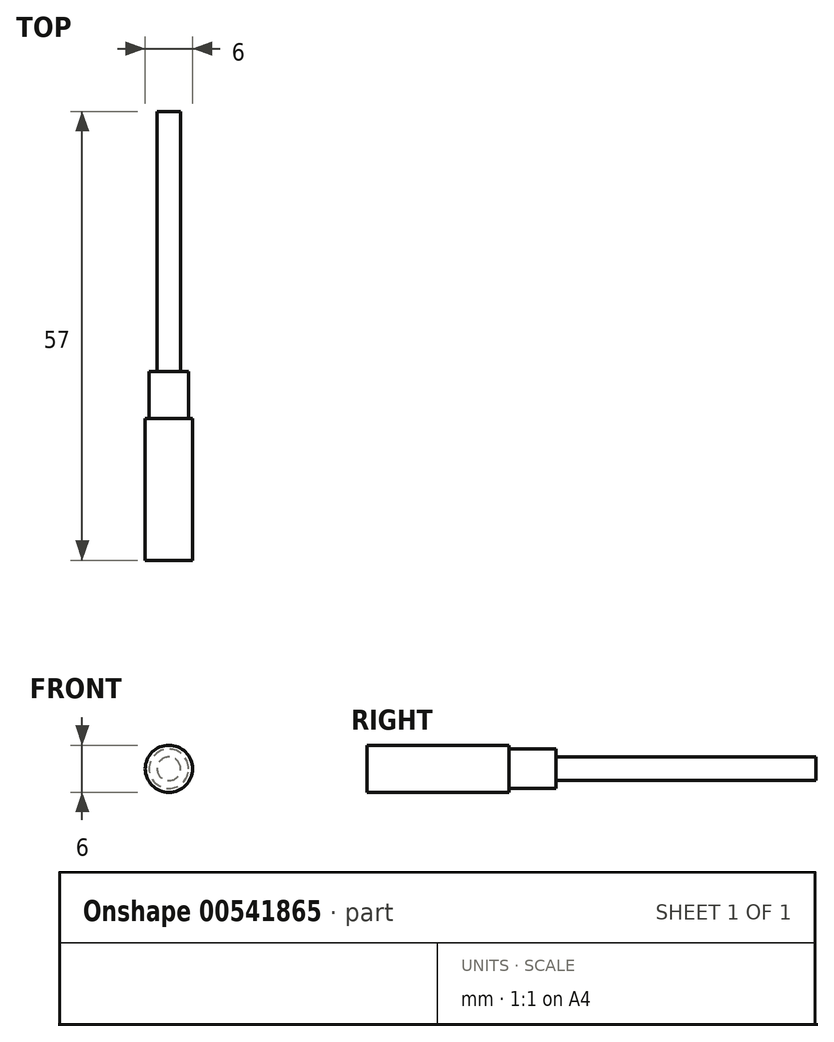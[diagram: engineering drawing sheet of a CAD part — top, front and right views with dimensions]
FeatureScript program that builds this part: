
annotation { "Feature Type Name" : "Feature", "Feature Type Description" : "" }
export const myFeature = defineFeature(function(context is Context, id is Id, definition is map)
    precondition{}
    {
        {
            var Q0;
            Q0=qCreatedBy(makeId("Front.planeOp"),FACE);
            var sketch = newSketch(context, id + "F0", { "sketchPlane" : qUnion([Q0])});
            skCircle(sketch, "E0", {"center": v(0, 0) * mm, "radius": 1.5 * mm});
            skSolve(sketch);
        }
        {
            var Q0;
            Q0=qSketchRegion(id+"F0",true);
            extrude(context, id + "F1", {"entities" : qUnion([Q0]), "depth" : 33 * mm, "offsetDistance" : 25 * mm});
        }
        {
            var Q0;
            Q0=makeQuery(id+"F1.opExtrude","CAP_FACE",FACE,{"disambiguationData":[OSD([sQuery(id+"F0.wireOp",EDGE,"E0")])],"isStart":false});
            var sketch = newSketch(context, id + "F2", { "sketchPlane" : qUnion([Q0])});
            skCircle(sketch, "E1", {"center": v(0, 0) * mm, "radius": 2.5 * mm});
            skSolve(sketch);
        }
        {
            var Q0;
            Q0=makeQuery(id+"F2.imprint","IMPRINT",FACE,{"disambiguationData":[TD([[makeQuery(id+"F2.imprint","IMPRINT",EDGE,{"derivedFrom":sQuery(id+"F2.wireOp",EDGE,"E1")}),1.0]])]});
            var Q1;
            Q1=makeQuery(id+"F2.imprint","IMPRINT",FACE,{"disambiguationData":[TD([[makeQuery(id+"F2.imprint","IMPRINT",EDGE,{"derivedFrom":makeQuery(id+"F1.opExtrude","CAP_EDGE",EDGE,{"disambiguationData":[OSD([sQuery(id+"F0.wireOp",EDGE,"E0")])],"isStart":false})}),1.0]])]});
            extrude(context, id + "F3", {"entities" : qUnion([Q0, Q1]), "operationType" : NewBodyOperationType.ADD, "depth" : 6 * mm, "offsetDistance" : 25 * mm});
        }
        {
            var Q0;
            Q0=makeQuery(id+"F3.opExtrude","CAP_FACE",FACE,{"disambiguationData":[OSD([sQuery(id+"F2.wireOp",EDGE,"E1")])],"isStart":false});
            var sketch = newSketch(context, id + "F4", { "sketchPlane" : qUnion([Q0])});
            skCircle(sketch, "E2", {"center": v(0, 0) * mm, "radius": 3 * mm});
            skSolve(sketch);
        }
        {
            var Q0;
            Q0=makeQuery(id+"F4.imprint","IMPRINT",FACE,{"disambiguationData":[TD([[makeQuery(id+"F4.imprint","IMPRINT",EDGE,{"derivedFrom":makeQuery(id+"F3.opExtrude","CAP_EDGE",EDGE,{"disambiguationData":[OSD([sQuery(id+"F2.wireOp",EDGE,"E1")])],"isStart":false})}),1.0]])]});
            var Q1;
            Q1=makeQuery(id+"F4.imprint","IMPRINT",FACE,{"disambiguationData":[TD([[makeQuery(id+"F4.imprint","IMPRINT",EDGE,{"derivedFrom":sQuery(id+"F4.wireOp",EDGE,"E2")}),1.0]])]});
            extrude(context, id + "F5", {"entities" : qUnion([Q0, Q1]), "operationType" : NewBodyOperationType.ADD, "depth" : 18 * mm, "offsetDistance" : 25 * mm});
        }
    });
